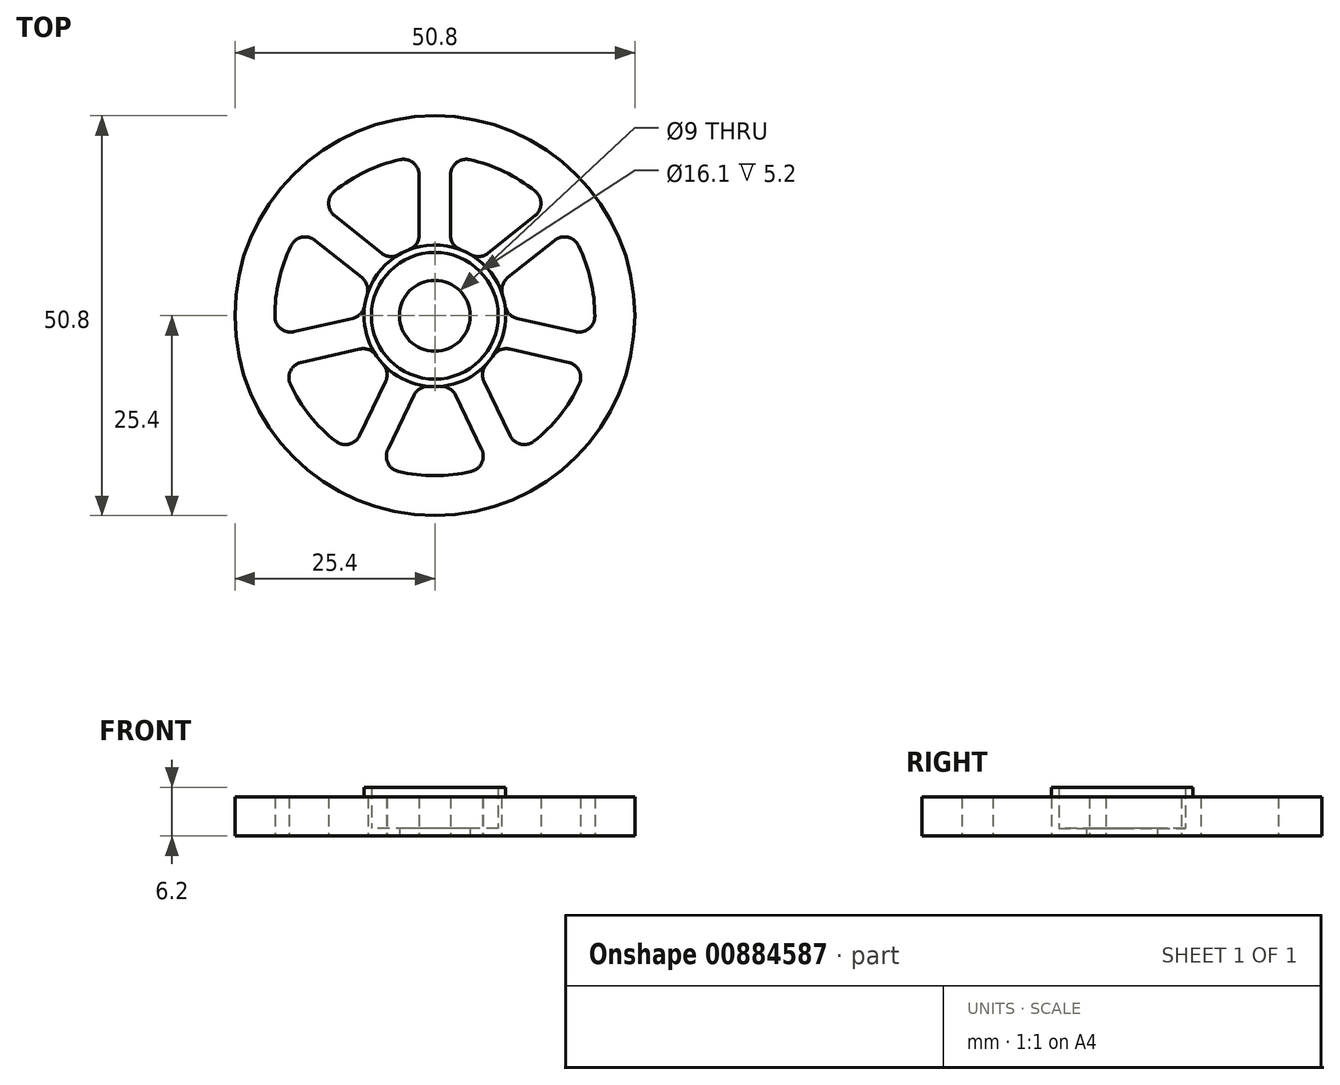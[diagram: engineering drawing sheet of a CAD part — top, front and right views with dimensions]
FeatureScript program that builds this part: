
annotation { "Feature Type Name" : "Feature", "Feature Type Description" : "" }
export const myFeature = defineFeature(function(context is Context, id is Id, definition is map)
    precondition{}
    {
        {
            var Q0;
            Q0=qCreatedBy(makeId("Top.planeOp"),FACE);
            var sketch = newSketch(context, id + "F0", { "sketchPlane" : qUnion([Q0])});
            skCircle(sketch, "E0", {"center": v(0, 0) * mm, "radius": 25.4 * mm});
            skCircle(sketch, "E1", {"center": v(0, 0) * mm, "radius": 4.5 * mm});
            skArc(sketch, "E2", {"start": v(-3.27, 8.38) * mm, "mid": v(-3.9, 8.1) * mm, "end": v(-4.51, 7.79) * mm});
            skCircle(sketch, "E3", {"center": v(0, 0) * mm, "radius": 8.1 * mm});
            skArc(sketch, "E4.0", {"start": v(-4.44, 19.83) * mm, "mid": v(-8.82, 18.3) * mm, "end": v(-12.74, 15.83) * mm});
            skLineSegment(sketch, "E5.0", {"start": v(-2, 17.88) * mm, "end": v(-2, 10.25) * mm});
            skLineSegment(sketch, "E6.0", {"start": v(2, 17.88) * mm, "end": v(2, 10.25) * mm});
            skPoint(sketch, "E7.orphan", {"position": v(0, 22.73) * mm});
            skPoint(sketch, "E8.visualSharp", {"position": v(-2, 20.22) * mm});
            skArc(sketch, "E8.filletArc", {"start": v(-2, 17.88) * mm, "mid": v(-2.75, 19.44) * mm, "end": v(-4.44, 19.83) * mm});
            skPoint(sketch, "E9.visualSharp", {"position": v(2, 20.22) * mm});
            skArc(sketch, "E9.filletArc", {"start": v(4.44, 19.83) * mm, "mid": v(2.75, 19.44) * mm, "end": v(2, 17.88) * mm});
            skPoint(sketch, "E10.visualSharp", {"position": v(2, 8.77) * mm});
            skArc(sketch, "E10.filletArc", {"start": v(2, 10.25) * mm, "mid": v(2.35, 9.12) * mm, "end": v(3.27, 8.38) * mm});
            skPoint(sketch, "E11.visualSharp", {"position": v(-2, 8.77) * mm});
            skArc(sketch, "E11.filletArc", {"start": v(-3.27, 8.38) * mm, "mid": v(-2.35, 9.12) * mm, "end": v(-2, 10.25) * mm});
            skLineSegment(sketch, "E12.1.0", {"start": v(-15.22, 9.58) * mm, "end": v(-9.26, 4.83) * mm});
            skArc(sketch, "E12.1.1", {"start": v(-8.6, 2.67) * mm, "mid": v(-8.6, 3.85) * mm, "end": v(-9.26, 4.83) * mm});
            skArc(sketch, "E12.1.2", {"start": v(-15.22, 9.58) * mm, "mid": v(-16.91, 9.97) * mm, "end": v(-18.27, 8.9) * mm});
            skArc(sketch, "E12.1.3", {"start": v(-12.74, 15.83) * mm, "mid": v(-13.48, 14.27) * mm, "end": v(-12.73, 12.71) * mm});
            skLineSegment(sketch, "E12.1.4", {"start": v(-12.73, 12.71) * mm, "end": v(-6.76, 7.95) * mm});
            skArc(sketch, "E12.1.5", {"start": v(-6.76, 7.95) * mm, "mid": v(-5.67, 7.52) * mm, "end": v(-4.51, 7.79) * mm});
            skLineSegment(sketch, "E12.2.0", {"start": v(-16.98, -5.93) * mm, "end": v(-9.54, -4.23) * mm});
            skArc(sketch, "E12.2.1", {"start": v(-7.45, -5.06) * mm, "mid": v(-8.37, -4.32) * mm, "end": v(-9.54, -4.23) * mm});
            skArc(sketch, "E12.2.2", {"start": v(-16.98, -5.93) * mm, "mid": v(-18.34, -7) * mm, "end": v(-18.35, -8.74) * mm});
            skArc(sketch, "E12.2.3", {"start": v(-20.32, -0.09) * mm, "mid": v(-19.56, -1.64) * mm, "end": v(-17.87, -2.03) * mm});
            skLineSegment(sketch, "E12.2.4", {"start": v(-17.87, -2.03) * mm, "end": v(-10.44, -0.33) * mm});
            skArc(sketch, "E12.2.5", {"start": v(-10.44, -0.33) * mm, "mid": v(-9.41, 0.26) * mm, "end": v(-8.9, 1.33) * mm});
            skLineSegment(sketch, "E12.3.0", {"start": v(-5.96, -16.98) * mm, "end": v(-2.64, -10.1) * mm});
            skArc(sketch, "E12.3.1", {"start": v(-0.69, -8.97) * mm, "mid": v(-1.84, -9.23) * mm, "end": v(-2.64, -10.1) * mm});
            skArc(sketch, "E12.3.2", {"start": v(-5.96, -16.98) * mm, "mid": v(-5.96, -18.7) * mm, "end": v(-4.6, -19.8) * mm});
            skArc(sketch, "E12.3.3", {"start": v(-12.6, -15.94) * mm, "mid": v(-10.91, -16.32) * mm, "end": v(-9.56, -15.24) * mm});
            skLineSegment(sketch, "E12.3.4", {"start": v(-9.56, -15.24) * mm, "end": v(-6.25, -8.36) * mm});
            skArc(sketch, "E12.3.5", {"start": v(-6.25, -8.36) * mm, "mid": v(-6.07, -7.2) * mm, "end": v(-6.59, -6.13) * mm});
            skLineSegment(sketch, "E12.4.0", {"start": v(9.56, -15.24) * mm, "end": v(6.25, -8.36) * mm});
            skArc(sketch, "E12.4.1", {"start": v(6.59, -6.13) * mm, "mid": v(6.07, -7.2) * mm, "end": v(6.25, -8.36) * mm});
            skArc(sketch, "E12.4.2", {"start": v(9.56, -15.24) * mm, "mid": v(10.91, -16.32) * mm, "end": v(12.6, -15.94) * mm});
            skArc(sketch, "E12.4.3", {"start": v(4.6, -19.8) * mm, "mid": v(5.96, -18.7) * mm, "end": v(5.96, -16.98) * mm});
            skLineSegment(sketch, "E12.4.4", {"start": v(5.96, -16.98) * mm, "end": v(2.64, -10.1) * mm});
            skArc(sketch, "E12.4.5", {"start": v(2.64, -10.1) * mm, "mid": v(1.84, -9.23) * mm, "end": v(0.69, -8.97) * mm});
            skLineSegment(sketch, "E12.5.0", {"start": v(17.87, -2.03) * mm, "end": v(10.44, -0.33) * mm});
            skArc(sketch, "E12.5.1", {"start": v(8.9, 1.33) * mm, "mid": v(9.41, 0.26) * mm, "end": v(10.44, -0.33) * mm});
            skArc(sketch, "E12.5.2", {"start": v(17.87, -2.03) * mm, "mid": v(19.56, -1.64) * mm, "end": v(20.32, -0.09) * mm});
            skArc(sketch, "E12.5.3", {"start": v(18.35, -8.74) * mm, "mid": v(18.34, -7) * mm, "end": v(16.98, -5.93) * mm});
            skLineSegment(sketch, "E12.5.4", {"start": v(16.98, -5.93) * mm, "end": v(9.54, -4.23) * mm});
            skArc(sketch, "E12.5.5", {"start": v(9.54, -4.23) * mm, "mid": v(8.37, -4.32) * mm, "end": v(7.45, -5.06) * mm});
            skLineSegment(sketch, "E12.6.0", {"start": v(12.73, 12.71) * mm, "end": v(6.76, 7.95) * mm});
            skArc(sketch, "E12.6.1", {"start": v(4.51, 7.79) * mm, "mid": v(5.67, 7.52) * mm, "end": v(6.76, 7.95) * mm});
            skArc(sketch, "E12.6.2", {"start": v(12.73, 12.71) * mm, "mid": v(13.48, 14.27) * mm, "end": v(12.74, 15.83) * mm});
            skArc(sketch, "E12.6.3", {"start": v(18.27, 8.9) * mm, "mid": v(16.91, 9.97) * mm, "end": v(15.22, 9.58) * mm});
            skLineSegment(sketch, "E12.6.4", {"start": v(15.22, 9.58) * mm, "end": v(9.26, 4.83) * mm});
            skArc(sketch, "E12.6.5", {"start": v(9.26, 4.83) * mm, "mid": v(8.6, 3.85) * mm, "end": v(8.6, 2.67) * mm});
            skArc(sketch, "E13.trimOffspring", {"start": v(-18.27, 8.9) * mm, "mid": v(-19.81, 4.52) * mm, "end": v(-20.32, -0.09) * mm});
            skArc(sketch, "E14.trimOffspring", {"start": v(-18.35, -8.74) * mm, "mid": v(-15.89, -12.67) * mm, "end": v(-12.6, -15.94) * mm});
            skArc(sketch, "E15.trimOffspring", {"start": v(-4.6, -19.8) * mm, "mid": v(0, -20.32) * mm, "end": v(4.6, -19.8) * mm});
            skArc(sketch, "E16.trimOffspring", {"start": v(12.6, -15.94) * mm, "mid": v(15.89, -12.67) * mm, "end": v(18.35, -8.74) * mm});
            skArc(sketch, "E17.trimOffspring", {"start": v(20.32, -0.09) * mm, "mid": v(19.81, 4.52) * mm, "end": v(18.27, 8.9) * mm});
            skArc(sketch, "E18.trimOffspring", {"start": v(12.74, 15.83) * mm, "mid": v(8.82, 18.3) * mm, "end": v(4.44, 19.83) * mm});
            skArc(sketch, "E19.trimOffspring", {"start": v(-8.6, 2.67) * mm, "mid": v(-8.77, 2) * mm, "end": v(-8.9, 1.33) * mm});
            skArc(sketch, "E20.trimOffspring", {"start": v(-7.45, -5.06) * mm, "mid": v(-7.04, -5.61) * mm, "end": v(-6.59, -6.13) * mm});
            skArc(sketch, "E21.trimOffspring", {"start": v(-0.69, -8.97) * mm, "mid": v(0, -9) * mm, "end": v(0.69, -8.97) * mm});
            skArc(sketch, "E22.trimOffspring", {"start": v(6.59, -6.13) * mm, "mid": v(7.04, -5.61) * mm, "end": v(7.45, -5.06) * mm});
            skArc(sketch, "E23.trimOffspring", {"start": v(8.9, 1.33) * mm, "mid": v(8.77, 2) * mm, "end": v(8.6, 2.67) * mm});
            skArc(sketch, "E24.trimOffspring", {"start": v(4.51, 7.79) * mm, "mid": v(3.9, 8.1) * mm, "end": v(3.27, 8.38) * mm});
            skSolve(sketch);
        }
        {
            var Q0;
            Q0=makeQuery(id+"F0.imprint","IMPRINT",FACE,{"disambiguationData":[TD([[makeQuery(id+"F0.imprint","IMPRINT",EDGE,{"derivedFrom":sQuery(id+"F0.wireOp",EDGE,"E1")}),1.0]])]});
            var sketch = newSketch(context, id + "F1", { "sketchPlane" : qUnion([Q0])});
            skCircle(sketch, "E25", {"center": v(0, 0) * mm, "radius": 9 * mm});
            skCircle(sketch, "E26", {"center": v(0, 0) * mm, "radius": 8.05 * mm});
            skSolve(sketch);
        }
        {
            var Q0;
            Q0=makeQuery(id+"F0.imprint","IMPRINT",FACE,{"disambiguationData":[TD([[makeQuery(id+"F0.imprint","IMPRINT",EDGE,{"derivedFrom":sQuery(id+"F0.wireOp",EDGE,"E0")}),1.0]])]});
            extrude(context, id + "F2", {"entities" : qUnion([Q0]), "depth" : 5 * mm, "offsetDistance" : 25.4 * mm});
        }
        {
            var Q0;
            Q0=makeQuery(id+"F1.imprint","IMPRINT",FACE,{"disambiguationData":[TD([[makeQuery(id+"F1.imprint","IMPRINT",EDGE,{"derivedFrom":sQuery(id+"F1.wireOp",EDGE,"E26")}),1.0]])]});
            extrude(context, id + "F3", {"entities" : qUnion([Q0]), "depth" : 1 * mm, "offsetDistance" : 25.4 * mm});
        }
        {
            var Q0;
            Q0 = qSketchRegion(id + "F1", true);
            extrude(context, id + "F4", {"entities" : qUnion([Q0]), "operationType" : NewBodyOperationType.ADD, "depth" : 6.2 * mm, "offsetDistance" : 25.4 * mm});
        }
    });
